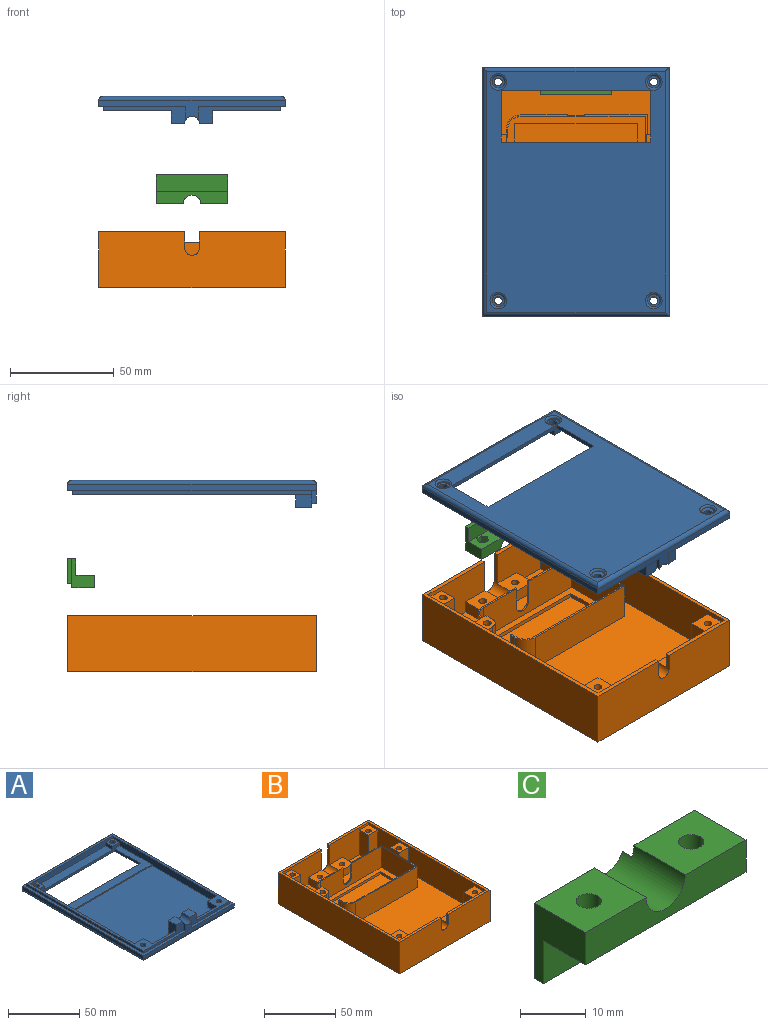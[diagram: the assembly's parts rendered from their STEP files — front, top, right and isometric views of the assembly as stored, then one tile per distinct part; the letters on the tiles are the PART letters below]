
ASSEMBLY  parts=3 mates=2
PART A: 59 faces, bbox 90x120x13 mm
  f0: cylinder r=1.9mm len=3.8mm, axis (0,0,-1), area 41.8mm2, adj f31,f50
  f1: cylinder r=1.9mm len=3.8mm, axis (0,0,-1), area 41.8mm2, adj f29,f47
  f2: plane 116x86mm, normal (0,0,-1), area 7974.9mm2, adj f24,f25,f26,f27,f51,f52,f53,f54
  f3: plane 7.8x6.5mm, normal (0,0,1), area 50.7mm2, adj f4,f38,f40,f44
  f4: plane 39.8x8mm, normal (0,-1,0), area 121mm2, adj f3,f13,f16,f18,f40,f43,f44
  f5: plane 31x6mm, normal (0,1,0), area 141mm2, adj f6,f7,f13,f36,f37,f40
  f6: plane 82x73.18mm, normal (0,0,1), area 5824.4mm2, adj f5,f7,f8,f9,f23,f38,f39,f40
  f7: plane 112x6mm, normal (-1,0,0), area 567.2mm2, adj f5,f6,f10,f12,f13,f23,f26,f31
  f8: plane 31x6mm, normal (0,1,0), area 141mm2, adj f6,f9,f13,f32,f34,f39
  f9: plane 112x6mm, normal (1,0,0), area 567.2mm2, adj f6,f8,f10,f12,f13,f23,f26,f29
  f10: plane 82x31.82mm, normal (0,0,1), area 809.1mm2, adj f7,f9,f23,f24,f25,f26,f27
  f11: plane 68x7mm, normal (0,0,1), area 476mm2, adj f12,f26,f28,f30
  f12: plane 82x5mm, normal (0,-1,0), area 368mm2, adj f7,f9,f11,f13,f28,f29,f30,f31
  f13: plane 115.6x85.6mm, normal (0,0,1), area 814.7mm2, adj f4,f5,f7,f8,f9,f12,f14,f15
  f14: plane 115.6x2mm, normal (-1,0,0), area 231.2mm2, adj f13,f15,f17,f18
  f15: plane 85.6x2mm, normal (0,1,0), area 171.2mm2, adj f13,f14,f16,f18
  f16: plane 115.6x2mm, normal (1,0,0), area 231.2mm2, adj f4,f13,f15,f18
  f17: plane 39.8x8mm, normal (0,-1,0), area 121mm2, adj f13,f14,f18,f39,f41,f42,f44
  f18: plane 120x90mm, normal (0,0,1), area 891.4mm2, adj f4,f14,f15,f16,f17,f19,f20,f21
  f19: plane 120x3mm, normal (1,0,0), area 360mm2, adj f18,f20,f22,f53
  f20: plane 90x9.2mm, normal (0,-1,0), area 300mm2, adj f18,f19,f21,f42,f43,f44,f54
  f21: plane 120x3mm, normal (-1,0,0), area 360mm2, adj f18,f20,f22,f52
  f22: plane 90x3mm, normal (0,1,0), area 270mm2, adj f18,f19,f21,f51
  f23: plane 82x1mm, normal (0,-1,0), area 82mm2, adj f6,f7,f9,f10
  f24: plane 72x2mm, normal (0,1,0), area 144mm2, adj f2,f10,f25,f27
  f25: plane 25x2mm, normal (-1,0,0), area 50mm2, adj f2,f10,f24,f26
  f26: plane 82x5mm, normal (0,-1,0), area 186mm2, adj f2,f7,f9,f10,f11,f25,f27,f28
  f27: plane 25x2mm, normal (1,0,0), area 50mm2, adj f2,f10,f24,f26
  f28: plane 7x3mm, normal (1,0,0), area 21mm2, adj f11,f12,f26,f29
  f29: plane 7x7mm, normal (0,0,1), area 37.7mm2, adj f1,f9,f12,f26,f28
  f30: plane 7x3mm, normal (-1,0,0), area 21mm2, adj f11,f12,f26,f31
  f31: plane 7x7mm, normal (0,0,1), area 37.7mm2, adj f0,f7,f12,f26,f30
  f32: plane 9x5mm, normal (1,0,0), area 45mm2, adj f8,f13,f33,f34
  f33: plane 9x5mm, normal (0,1,0), area 45mm2, adj f9,f13,f32,f34
  f34: plane 9x9mm, normal (0,0,-1), area 69.7mm2, adj f8,f9,f32,f33,f46
  f35: plane 9x5mm, normal (0,1,0), area 45mm2, adj f7,f13,f36,f37
  f36: plane 9x5mm, normal (-1,0,0), area 45mm2, adj f5,f13,f35,f37
  f37: plane 9x9mm, normal (0,0,-1), area 69.7mm2, adj f5,f7,f35,f36,f45
  f38: plane 20x12mm, normal (0,1,0), area 220.8mm2, adj f3,f6,f39,f40,f41,f44
  f39: plane 12x7.8mm, normal (-1,0,0), area 82.8mm2, adj f6,f8,f13,f17,f38,f41
  f40: plane 12x7.8mm, normal (1,0,0), area 82.8mm2, adj f3,f4,f5,f6,f13,f38
  f41: plane 7.8x6.5mm, normal (0,0,1), area 50.7mm2, adj f17,f38,f39,f44
  f42: plane 6.2x2.2mm, normal (-1,0,0), area 13.6mm2, adj f17,f18,f20,f44
  f43: plane 6.2x2.2mm, normal (1,0,0), area 13.6mm2, adj f4,f18,f20,f44
  f44: cylinder r=3.5mm len=10mm, axis (0,1,0), area 101.6mm2, adj f3,f4,f17,f20,f38,f41,f42,f43
  f45: cylinder r=1.9mm len=5mm, axis (0,0,-1), area 59.7mm2, adj f13,f37
  f46: cylinder r=1.9mm len=5mm, axis (0,0,-1), area 59.7mm2, adj f13,f34
  f47: plane 6x6mm, normal (0,0,-1), area 16.9mm2, adj f1,f48
  f48: cylinder r=3mm len=6mm, axis (0,0,-1), area 9.4mm2, adj f47,f55
  f49: cylinder r=3mm len=6mm, axis (0,0,-1), area 9.4mm2, adj f50,f57
  f50: plane 6x6mm, normal (0,0,-1), area 16.9mm2, adj f0,f49
  f51: cylinder r=2mm len=90mm, axis (-1,0,0), area 278.2mm2, adj f2,f22,f52,f53
  f52: cylinder r=2mm len=120mm, axis (0,-1,0), area 372.4mm2, adj f2,f21,f51,f54
  f53: cylinder r=2mm len=120mm, axis (0,1,0), area 372.4mm2, adj f2,f19,f51,f54
  f54: cylinder r=2mm len=90mm, axis (1,0,0), area 278.2mm2, adj f2,f20,f52,f53
  f55: torus R=4mm, axis (0,0,1), area 33.2mm2, adj f2,f48
  f56: torus R=4mm, axis (0,0,1), area 33.2mm2, adj f2,f6
  f57: torus R=4mm, axis (0,0,1), area 33.2mm2, adj f2,f49
  f58: torus R=4mm, axis (0,0,1), area 33.2mm2, adj f2,f6
PART B: 143 faces, bbox 90x120x27 mm
  f0: plane 39.5x23mm, normal (0,1,0), area 580mm2, adj f2,f3,f17,f22,f36,f37,f137,f140
  f1: plane 120x41.5mm, normal (0,0,1), area 396.6mm2, adj f4,f16,f23,f29,f30,f31,f60,f141
  f2: plane 6.5x6mm, normal (0,0,1), area 39mm2, adj f0,f136,f137,f142
  f3: plane 94.4x86mm, normal (0,0,1), area 5750.8mm2, adj f0,f4,f16,f17,f19,f25,f32,f33
  f4: plane 39.5x23mm, normal (0,1,0), area 580mm2, adj f1,f3,f16,f33,f34,f138,f139,f141
  f5: plane 120x90mm, normal (0,0,-1), area 10612.9mm2, adj f23,f28,f29,f30,f81,f82,f83,f84
  f6: cylinder r=1.9mm len=4mm, axis (0,0,-1), area 47.8mm2, adj f27,f129
  f7: cylinder r=1.9mm len=4mm, axis (0,0,-1), area 47.8mm2, adj f21,f128
  f8: cylinder r=1.9mm len=10mm, axis (0,0,-1), area 119.4mm2, adj f37,f115
  f9: cylinder r=1.9mm len=10mm, axis (0,0,-1), area 119.4mm2, adj f34,f108
  f10: cylinder r=1.9mm len=10mm, axis (0,0,1), area 119.4mm2, adj f74,f101
  f11: cylinder r=1.9mm len=10mm, axis (0,0,1), area 119.4mm2, adj f70,f94
  f12: cylinder r=1.9mm len=10mm, axis (0,0,1), area 119.4mm2, adj f67,f87
  f13: cylinder r=1.9mm len=10mm, axis (0,0,1), area 119.4mm2, adj f63,f80
  f14: plane 18x9.2mm, normal (1,0,0), area 165.6mm2, adj f15,f24,f26,f72
  f15: plane 86x30mm, normal (0,0,1), area 1423.4mm2, adj f14,f16,f17,f20,f24,f31,f38,f39
  f16: plane 116x23mm, normal (-1,0,0), area 2059mm2, adj f1,f3,f4,f15,f31,f32,f34,f69
  f17: plane 116x23mm, normal (1,0,0), area 2059mm2, adj f0,f3,f15,f20,f22,f35,f37,f61
  f18: plane 29.5x10.8mm, normal (0,0,1), area 28.5mm2, adj f19,f24,f25,f47,f48,f56,f65,f66
  f19: plane 18x0.6mm, normal (0,-1,0), area 10.8mm2, adj f3,f18,f48,f65
  f20: plane 38.92x23mm, normal (0,-1,0), area 625.1mm2, adj f15,f17,f22,f27,f40,f58,f59,f62
  f21: plane 13.17x11mm, normal (0,0,1), area 133.5mm2, adj f7,f31,f38,f39,f58
  f22: plane 120x41.5mm, normal (0,0,1), area 396.6mm2, adj f0,f17,f20,f23,f28,f29,f59,f140
  f23: plane 90x27mm, normal (0,1,0), area 2267.9mm2, adj f1,f5,f22,f28,f30,f58,f59,f60
  f24: plane 61x18mm, normal (0,1,0), area 977.9mm2, adj f14,f15,f18,f26,f55,f56,f57,f77
  f25: plane 60.4x18mm, normal (0,-1,0), area 967.1mm2, adj f3,f18,f26,f49,f55,f56,f57,f75
  f26: plane 68x36mm, normal (0,0,1), area 107.9mm2, adj f14,f24,f25,f46,f49,f50,f51,f52
  f27: plane 13.17x11mm, normal (0,0,1), area 133.5mm2, adj f6,f20,f38,f40,f58
  f28: plane 120x27mm, normal (-1,0,0), area 3240mm2, adj f5,f22,f23,f29
  f29: plane 90x27mm, normal (0,-1,0), area 2355mm2, adj f1,f5,f22,f28,f30,f140,f141,f142
  f30: plane 120x27mm, normal (1,0,0), area 3240mm2, adj f1,f5,f23,f29
  f31: plane 38.92x23mm, normal (0,-1,0), area 625.1mm2, adj f1,f15,f16,f21,f39,f58,f60,f68
  f32: plane 21x11mm, normal (0,1,0), area 231mm2, adj f3,f16,f33,f34
  f33: plane 21x11mm, normal (-1,0,0), area 231mm2, adj f3,f4,f32,f34
  f34: plane 11x11mm, normal (0,0,1), area 109.7mm2, adj f4,f9,f16,f32,f33
  f35: plane 21x11mm, normal (0,1,0), area 231mm2, adj f3,f17,f36,f37
  f36: plane 21x11mm, normal (1,0,0), area 231mm2, adj f0,f3,f35,f37
  f37: plane 11x11mm, normal (0,0,1), area 109.7mm2, adj f0,f8,f17,f35,f36
  f38: plane 34.5x6mm, normal (0,-1,0), area 187.6mm2, adj f15,f21,f27,f39,f40,f58
  f39: plane 11x6mm, normal (1,0,0), area 66mm2, adj f15,f21,f31,f38
  f40: plane 11x6mm, normal (-1,0,0), area 66mm2, adj f15,f20,f27,f38
  f41: plane 59x2mm, normal (0,-1,0), area 118mm2, adj f3,f42,f44,f45
  f42: plane 27x2mm, normal (1,0,0), area 54mm2, adj f3,f41,f43,f45
  f43: plane 59x2mm, normal (0,1,0), area 118mm2, adj f3,f42,f44,f45
  f44: plane 27x2mm, normal (-1,0,0), area 54mm2, adj f3,f41,f43,f45
  f45: plane 59x27mm, normal (0,0,1), area 1593mm2, adj f41,f42,f43,f44
  f46: plane 18x17.8mm, normal (1,0,0), area 320.4mm2, adj f3,f26,f54,f71
  f47: plane 18x2.2mm, normal (-1,0,0), area 39.6mm2, adj f15,f18,f66,f77
  f48: plane 18x4mm, normal (1,0,0), area 72mm2, adj f3,f18,f19,f75
  f49: plane 34.4x18mm, normal (-1,0,0), area 619.2mm2, adj f3,f25,f26,f50
  f50: plane 60.4x18mm, normal (0,1,0), area 1087.2mm2, adj f3,f26,f49,f76
  f51: plane 18x3.2mm, normal (1,0,0), area 57.6mm2, adj f3,f26,f52,f76
  f52: plane 18x0.8mm, normal (0,1,0), area 14.4mm2, adj f3,f26,f51,f53
  f53: plane 18x3mm, normal (-1,0,0), area 54mm2, adj f3,f26,f52,f78
  f54: plane 61x18mm, normal (0,-1,0), area 1098mm2, adj f3,f26,f46,f78
  f55: plane 11x0.8mm, normal (-1,0,0), area 8.8mm2, adj f24,f25,f26,f57
  f56: plane 11x0.8mm, normal (1,0,0), area 8.8mm2, adj f18,f24,f25,f57
  f57: cylinder r=4.2mm len=8.4mm, axis (0,1,0), area 10.6mm2, adj f24,f25,f55,f56
  f58: cylinder r=4.2mm len=13mm, axis (0,1,0), area 149.3mm2, adj f20,f21,f23,f27,f31,f38,f59,f60
  f59: plane 16x2mm, normal (1,0,0), area 32mm2, adj f20,f22,f23,f58
  f60: plane 16x2mm, normal (-1,0,0), area 32mm2, adj f1,f23,f31,f58
  f61: plane 21x9mm, normal (0,-1,0), area 189mm2, adj f15,f17,f62,f63
  f62: plane 21x9mm, normal (1,0,0), area 189mm2, adj f15,f20,f61,f63
  f63: plane 9x9mm, normal (0,0,1), area 69.7mm2, adj f13,f17,f20,f61,f62
  f64: plane 21x5mm, normal (0,-1,0), area 105mm2, adj f3,f17,f67,f79
  f65: plane 21x4.5mm, normal (1,0,0), area 65.7mm2, adj f3,f18,f19,f66,f67,f79
  f66: plane 21x9.5mm, normal (0,1,0), area 195.9mm2, adj f15,f17,f18,f47,f65,f67
  f67: plane 9.5x9mm, normal (0,0,1), area 69.8mm2, adj f12,f17,f64,f65,f66,f79
  f68: plane 21x9mm, normal (-1,0,0), area 189mm2, adj f15,f31,f69,f70
  f69: plane 21x9mm, normal (0,-1,0), area 189mm2, adj f15,f16,f68,f70
  f70: plane 9x9mm, normal (0,0,1), area 69.7mm2, adj f11,f16,f31,f68,f69
  f71: plane 21x9mm, normal (0,-1,0), area 183.6mm2, adj f3,f16,f26,f46,f73,f74
  f72: plane 21x9mm, normal (0,1,0), area 183.6mm2, adj f14,f15,f16,f26,f73,f74
  f73: plane 9x3mm, normal (-1,0,0), area 27mm2, adj f26,f71,f72,f74
  f74: plane 9x9mm, normal (0,0,1), area 69.7mm2, adj f10,f16,f71,f72,f73
  f75: cylinder r=6mm len=18mm, axis (0,0,1), area 169.6mm2, adj f3,f18,f25,f48
  f76: cylinder r=6mm len=18mm, axis (0,0,1), area 169.6mm2, adj f3,f26,f50,f51
  f77: cylinder r=7mm len=18mm, axis (0,0,-1), area 197.9mm2, adj f15,f18,f24,f47
  f78: cylinder r=7mm len=18mm, axis (0,0,-1), area 197.9mm2, adj f3,f26,f53,f54
  f79: cylinder r=4.5mm len=21mm, axis (0,0,-1), area 148.4mm2, adj f3,f64,f65,f67
  f80: plane 6x5.2mm, normal (0,0,-1), area 12mm2, adj f13,f81,f82,f83,f84,f85,f86
  f81: plane 15x2.6mm, normal (-0.87,-0.5,0), area 45mm2, adj f5,f80,f82,f86
  f82: plane 15x2.6mm, normal (-0.87,0.5,0), area 45mm2, adj f5,f80,f81,f83
  f83: plane 15x3mm, normal (0,1,0), area 45mm2, adj f5,f80,f82,f84
  f84: plane 15x2.6mm, normal (0.87,0.5,0), area 45mm2, adj f5,f80,f83,f85
  f85: plane 15x2.6mm, normal (0.87,-0.5,0), area 45mm2, adj f5,f80,f84,f86
  f86: plane 15x3mm, normal (0,-1,0), area 45mm2, adj f5,f80,f81,f85
  f87: plane 6x5.2mm, normal (0,0,-1), area 12mm2, adj f12,f88,f89,f90,f91,f92,f93
  f88: plane 15x2.6mm, normal (-0.87,-0.5,0), area 45mm2, adj f5,f87,f89,f93
  f89: plane 15x2.6mm, normal (-0.87,0.5,0), area 45mm2, adj f5,f87,f88,f90
  f90: plane 15x3mm, normal (0,1,0), area 45mm2, adj f5,f87,f89,f91
  f91: plane 15x2.6mm, normal (0.87,0.5,0), area 45mm2, adj f5,f87,f90,f92
  f92: plane 15x2.6mm, normal (0.87,-0.5,0), area 45mm2, adj f5,f87,f91,f93
  f93: plane 15x3mm, normal (0,-1,0), area 45mm2, adj f5,f87,f88,f92
  f94: plane 6x5.2mm, normal (0,0,-1), area 12mm2, adj f11,f95,f96,f97,f98,f99,f100
  f95: plane 15x2.6mm, normal (-0.87,-0.5,0), area 45mm2, adj f5,f94,f96,f100
  f96: plane 15x2.6mm, normal (-0.87,0.5,0), area 45mm2, adj f5,f94,f95,f97
  f97: plane 15x3mm, normal (0,1,0), area 45mm2, adj f5,f94,f96,f98
  f98: plane 15x2.6mm, normal (0.87,0.5,0), area 45mm2, adj f5,f94,f97,f99
  f99: plane 15x2.6mm, normal (0.87,-0.5,0), area 45mm2, adj f5,f94,f98,f100
  f100: plane 15x3mm, normal (0,-1,0), area 45mm2, adj f5,f94,f95,f99
  f101: plane 6x5.2mm, normal (0,0,-1), area 12mm2, adj f10,f102,f103,f104,f105,f106,f107
  f102: plane 15x2.6mm, normal (-0.87,-0.5,0), area 45mm2, adj f5,f101,f103,f107
  f103: plane 15x2.6mm, normal (-0.87,0.5,0), area 45mm2, adj f5,f101,f102,f104
  f104: plane 15x3mm, normal (0,1,0), area 45mm2, adj f5,f101,f103,f105
  f105: plane 15x2.6mm, normal (0.87,0.5,0), area 45mm2, adj f5,f101,f104,f106
  f106: plane 15x2.6mm, normal (0.87,-0.5,0), area 45mm2, adj f5,f101,f105,f107
  f107: plane 15x3mm, normal (0,-1,0), area 45mm2, adj f5,f101,f102,f106
  f108: plane 6x5.2mm, normal (0,0,-1), area 12mm2, adj f9,f109,f110,f111,f112,f113,f114
  f109: plane 15x2.6mm, normal (0.87,-0.5,0), area 45mm2, adj f5,f108,f110,f114
  f110: plane 15x3mm, normal (0,-1,0), area 45mm2, adj f5,f108,f109,f111
  f111: plane 15x2.6mm, normal (-0.87,-0.5,0), area 45mm2, adj f5,f108,f110,f112
  f112: plane 15x2.6mm, normal (-0.87,0.5,0), area 45mm2, adj f5,f108,f111,f113
  f113: plane 15x3mm, normal (0,1,0), area 45mm2, adj f5,f108,f112,f114
  f114: plane 15x2.6mm, normal (0.87,0.5,0), area 45mm2, adj f5,f108,f109,f113
  f115: plane 6x5.2mm, normal (0,0,-1), area 12mm2, adj f8,f116,f117,f118,f119,f120,f121
  f116: plane 15x2.6mm, normal (-0.87,-0.5,0), area 45mm2, adj f5,f115,f117,f121
  f117: plane 15x2.6mm, normal (-0.87,0.5,0), area 45mm2, adj f5,f115,f116,f118
  f118: plane 15x3mm, normal (0,1,0), area 45mm2, adj f5,f115,f117,f119
  f119: plane 15x2.6mm, normal (0.87,0.5,0), area 45mm2, adj f5,f115,f118,f120
  f120: plane 15x2.6mm, normal (0.87,-0.5,0), area 45mm2, adj f5,f115,f119,f121
  f121: plane 15x3mm, normal (0,-1,0), area 45mm2, adj f5,f115,f116,f120
  f122: plane 6x2.6mm, normal (-0.87,-0.5,0), area 18mm2, adj f5,f123,f127,f128
  f123: plane 6x2.6mm, normal (-0.87,0.5,0), area 18mm2, adj f5,f122,f124,f128
  f124: plane 6x3mm, normal (0,1,0), area 18mm2, adj f5,f123,f125,f128
  f125: plane 6x2.6mm, normal (0.87,0.5,0), area 18mm2, adj f5,f124,f126,f128
  f126: plane 6x2.6mm, normal (0.87,-0.5,0), area 18mm2, adj f5,f125,f127,f128
  f127: plane 6x3mm, normal (0,-1,0), area 18mm2, adj f5,f122,f126,f128
  f128: plane 6x5.2mm, normal (0,0,-1), area 12mm2, adj f7,f122,f123,f124,f125,f126,f127
  f129: plane 6x5.2mm, normal (0,0,-1), area 12mm2, adj f6,f130,f131,f132,f133,f134,f135
  f130: plane 6x2.6mm, normal (0.87,0.5,0), area 18mm2, adj f5,f129,f131,f135
  f131: plane 6x2.6mm, normal (0.87,-0.5,0), area 18mm2, adj f5,f129,f130,f132
  f132: plane 6x3mm, normal (0,-1,0), area 18mm2, adj f5,f129,f131,f133
  f133: plane 6x2.6mm, normal (-0.87,-0.5,0), area 18mm2, adj f5,f129,f132,f134
  f134: plane 6x2.6mm, normal (-0.87,0.5,0), area 18mm2, adj f5,f129,f133,f135
  f135: plane 6x3mm, normal (0,1,0), area 18mm2, adj f5,f129,f130,f134
  f136: plane 20x15mm, normal (0,1,0), area 281mm2, adj f2,f3,f137,f138,f139,f142
  f137: plane 15x6mm, normal (-1,0,0), area 90mm2, adj f0,f2,f3,f136
  f138: plane 15x6mm, normal (1,0,0), area 90mm2, adj f3,f4,f136,f139
  f139: plane 6.5x6mm, normal (0,0,1), area 39mm2, adj f4,f136,f138,f142
  f140: plane 7.96x2mm, normal (1,0,0), area 15.9mm2, adj f0,f22,f29,f142
  f141: plane 7.99x2mm, normal (-1,0,0), area 16mm2, adj f1,f4,f29,f142
  f142: cylinder r=3.5mm len=8mm, axis (0,-1,0), area 87.4mm2, adj f0,f2,f4,f29,f136,f139,f140,f141
PART C: 30 faces, bbox 34.5x13x14 mm
  f0: plane 34.5x9mm, normal (0,0,-1), area 263.7mm2, adj f5,f7,f9,f11,f16,f17,f18,f19
  f1: cylinder r=1.9mm len=3.8mm, axis (0,0,-1), area 35.8mm2, adj f10,f23
  f2: cylinder r=1.9mm len=3.8mm, axis (0,0,-1), area 35.8mm2, adj f4,f22
  f3: plane 14x13.5mm, normal (0,1,0), area 188.4mm2, adj f6,f9,f10,f12,f13
  f4: plane 13.05x11mm, normal (0,0,1), area 132.2mm2, adj f2,f5,f7,f8,f12
  f5: plane 34.5x6mm, normal (0,-1,0), area 179.3mm2, adj f0,f4,f7,f9,f10,f12
  f6: plane 34.5x4mm, normal (0,0,-1), area 84mm2, adj f3,f7,f8,f9,f11,f13,f14,f15
  f7: plane 14x11mm, normal (1,0,0), area 82mm2, adj f0,f4,f5,f6,f8,f11
  f8: plane 14x13.5mm, normal (0,1,0), area 188.4mm2, adj f4,f6,f7,f12,f14
  f9: plane 14x11mm, normal (-1,0,0), area 82mm2, adj f0,f3,f5,f6,f10,f11
  f10: plane 13.05x11mm, normal (0,0,1), area 132.2mm2, adj f1,f3,f5,f9,f12
  f11: plane 34.5x8mm, normal (0,-1,0), area 276mm2, adj f0,f6,f7,f9
  f12: cylinder r=4.2mm len=13mm, axis (0,-1,0), area 163.7mm2, adj f3,f4,f5,f8,f10,f13,f14,f15
  f13: plane 12.11x2mm, normal (-1,0,0), area 24.2mm2, adj f3,f6,f12,f15
  f14: plane 12.11x2mm, normal (1,0,0), area 24.2mm2, adj f6,f8,f12,f15
  f15: plane 12.11x7.5mm, normal (0,1,0), area 78.4mm2, adj f6,f12,f13,f14
  f16: plane 3x2.6mm, normal (0.87,0.5,0), area 9mm2, adj f0,f17,f21,f22
  f17: plane 3x2.6mm, normal (0.87,-0.5,0), area 9mm2, adj f0,f16,f18,f22
  f18: plane 3x3mm, normal (0,-1,0), area 9mm2, adj f0,f17,f19,f22
  f19: plane 3x2.6mm, normal (-0.87,-0.5,0), area 9mm2, adj f0,f18,f20,f22
  f20: plane 3x2.6mm, normal (-0.87,0.5,0), area 9mm2, adj f0,f19,f21,f22
  f21: plane 3x3mm, normal (0,1,0), area 9mm2, adj f0,f16,f20,f22
  f22: plane 6x5.2mm, normal (0,0,-1), area 12mm2, adj f2,f16,f17,f18,f19,f20,f21
  f23: plane 6x5.2mm, normal (0,0,-1), area 12mm2, adj f1,f24,f25,f26,f27,f28,f29
  f24: plane 3x2.6mm, normal (-0.87,-0.5,0), area 9mm2, adj f0,f23,f25,f29
  f25: plane 3x2.6mm, normal (-0.87,0.5,0), area 9mm2, adj f0,f23,f24,f26
  f26: plane 3x3mm, normal (0,1,0), area 9mm2, adj f0,f23,f25,f27
  f27: plane 3x2.6mm, normal (0.87,0.5,0), area 9mm2, adj f0,f23,f26,f28
  f28: plane 3x2.6mm, normal (0.87,-0.5,0), area 9mm2, adj f0,f23,f27,f29
  f29: plane 3x3mm, normal (0,-1,0), area 9mm2, adj f0,f23,f24,f28
PLACE A rot(axis=(0,1,0),180deg) t=(0,0.33,92.29)mm
PLACE B t=(0,0.33,0)mm
PLACE C rot(axis=(0,1,0),180deg) t=(0,57.83,54.4)mm
MATE slider B.f7 <-> C.f1  axis (0,0,1) through (11,52.83,10)mm
MATE slider B.f11 <-> A.f1  axis (0,0,1) through (37.5,53.33,25)mm
